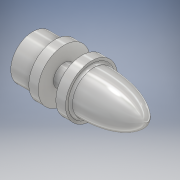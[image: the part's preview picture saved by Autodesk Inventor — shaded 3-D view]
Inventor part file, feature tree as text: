
AUTODESK INVENTOR PART (.ipt)
format: ipt  version: 2017 (Build 210142000, 142)  size: 220,160 bytes
history: native  units: mm
features: sketch x2, other x1, revolve x1, fillet x1, hole x1
ambient origin geometry x8: Origin, YZ Plane, XZ Plane, XY Plane, X Axis, Y Axis, Z Axis, Center Point
bodies: Body1 (feature_tree)
feature tree (6):
  other  "Bryła1"
  revolve  "Obrót1"
  fillet  "Zaokrąglenie1"  Radius=10.0mm
  hole  "Otwór1"  [1 undecoded]
  sketch  "Szkic1"
  sketch  "Szkic2"
note: 1 required parameter value undecoded (feature->parameter linkage not recoverable at this tier; creation-order binding heuristic only, values carry confidence <= 0.55)
